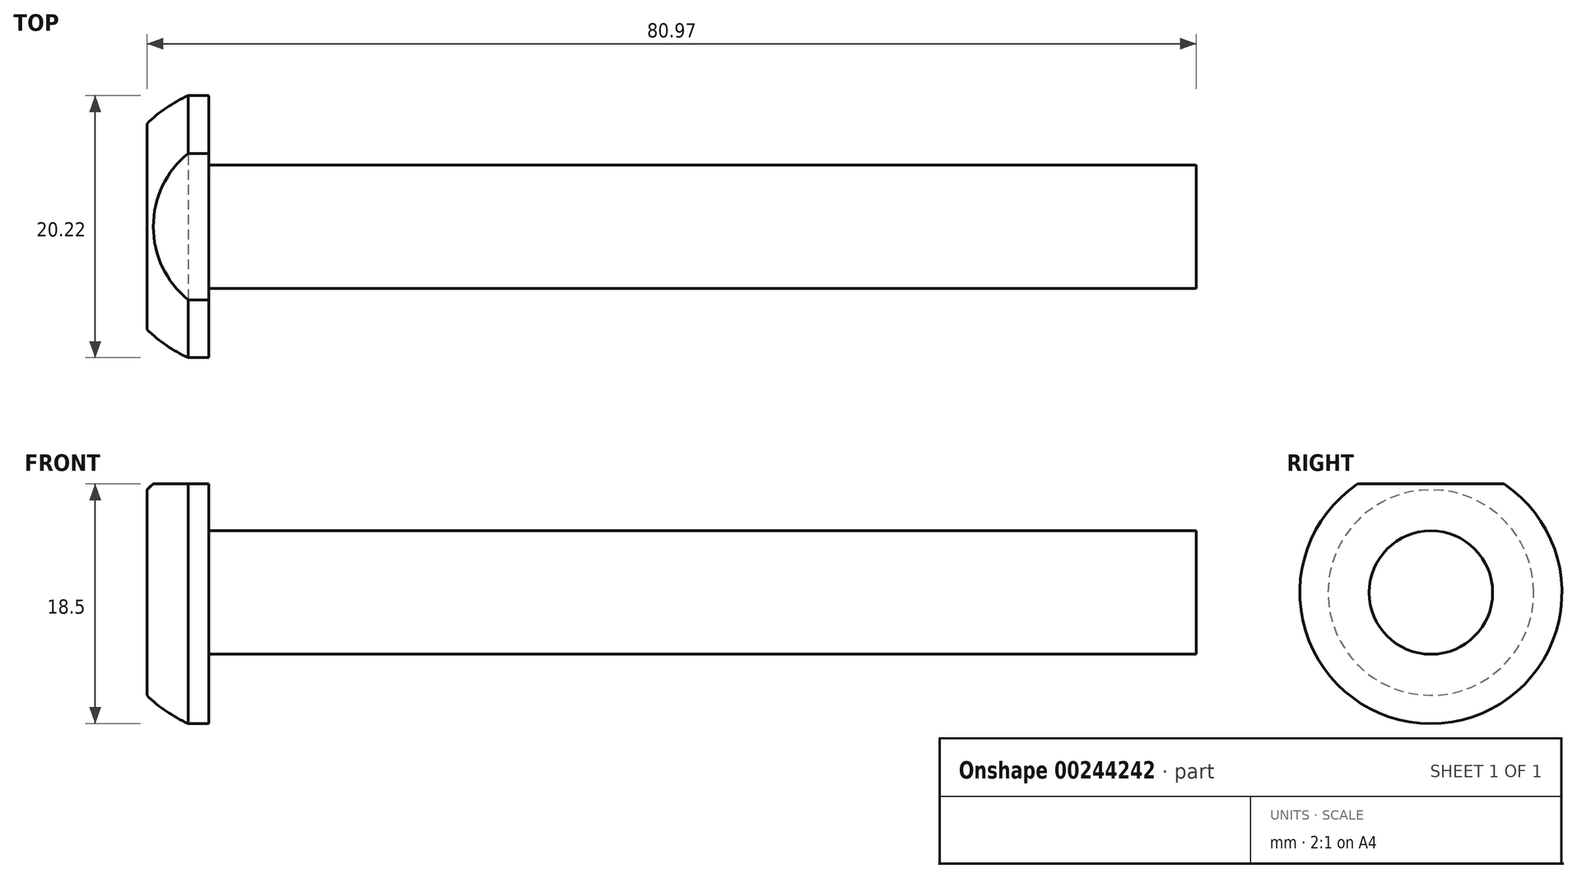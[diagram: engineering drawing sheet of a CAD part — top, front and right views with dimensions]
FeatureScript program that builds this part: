
annotation { "Feature Type Name" : "Feature", "Feature Type Description" : "" }
export const myFeature = defineFeature(function(context is Context, id is Id, definition is map)
    precondition{}
    {
        {
            var Q0;
            Q0=qCreatedBy(makeId("Front.planeOp"),FACE);
            var sketch = newSketch(context, id + "F0", { "sketchPlane" : qUnion([Q0])});
            skLineSegment(sketch, "E0.bottom", {"start": v(-52.41, 0) * mm, "end": v(23.79, 0) * mm});
            skLineSegment(sketch, "E0.top", {"start": v(-52.41, 4.76) * mm, "end": v(23.79, 4.76) * mm});
            skLineSegment(sketch, "E0.right", {"start": v(23.79, 0) * mm, "end": v(23.79, 4.76) * mm});
            skLineSegment(sketch, "E1.bottom", {"start": v(-52.41, 0) * mm, "end": v(-54, 0) * mm});
            skLineSegment(sketch, "E1.left", {"start": v(-52.41, 4.76) * mm, "end": v(-52.41, 7.94) * mm});
            skLineSegment(sketch, "E2.bottom", {"start": v(-52.41, 0) * mm, "end": v(-57.18, 0) * mm});
            skLineSegment(sketch, "E2.right", {"start": v(-57.18, 0) * mm, "end": v(-57.18, 7.94) * mm});
            skLineSegment(sketch, "E3", {"start": v(-54, 7.94) * mm, "end": v(-54, 10.11) * mm});
            skLineSegment(sketch, "E4", {"start": v(-52.41, 7.94) * mm, "end": v(-52.41, 10.11) * mm});
            skLineSegment(sketch, "E5", {"start": v(-54, 10.11) * mm, "end": v(-52.41, 10.11) * mm});
            skPoint(sketch, "E6.start.orphan", {"position": v(-54, 10.7) * mm});
            skArc(sketch, "E7.trimOffspring", {"start": v(-54, 10.11) * mm, "mid": v(-55.68, 9.16) * mm, "end": v(-57.18, 7.94) * mm});
            skLineSegment(sketch, "E8", {"start": v(-54, 7.94) * mm, "end": v(-54, 0) * mm});
            skSolve(sketch);
        }
        {
            var Q0;
            {var subQ0=sQuery(id+"F0.wireOp",EDGE,"E2.right");Q0=makeQuery(id+"F0.imprint","IMPRINT",FACE,{"disambiguationData":[TD([[makeQuery(id+"F0.imprint","IMPRINT",EDGE,{"derivedFrom":subQ0}),-1.0]])]});}
            var Q1;
            {var subQ1=sQuery(id+"F0.wireOp",EDGE,"E0.bottom");Q1=makeQuery(id+"F0.imprint","IMPRINT",FACE,{"disambiguationData":[TD([[makeQuery(id+"F0.imprint","IMPRINT",EDGE,{"derivedFrom":subQ1}),1.0]])]});}
            var Q2;
            Q2=sQuery(id+"F0.wireOp",EDGE,"E0.bottom");
            revolve(context, id + "F1", {"entities" : qUnion([Q0, Q1]), "axis" : qUnion([Q2]), "revolveType" : RevolveType.FULL});
        }
        {
            var Q0;
            Q0=makeQuery(id+"F1.opRevolve","SWEPT_FACE",FACE,{"disambiguationData":[OSD([sQuery(id+"F0.wireOp",EDGE,"E1.left"),sQuery(id+"F0.wireOp",EDGE,"E4")])]});
            var sketch = newSketch(context, id + "F2", { "sketchPlane" : qUnion([Q0])});
            skLineSegment(sketch, "E9.bottom", {"start": v(-5.65, 8.39) * mm, "end": v(6.31, 8.39) * mm});
            skLineSegment(sketch, "E9.top", {"start": v(-5.65, 10.42) * mm, "end": v(6.31, 10.42) * mm});
            skLineSegment(sketch, "E9.left", {"start": v(-5.65, 8.39) * mm, "end": v(-5.65, 10.42) * mm});
            skLineSegment(sketch, "E9.right", {"start": v(6.31, 8.39) * mm, "end": v(6.31, 10.42) * mm});
            skSolve(sketch);
        }
        {
            var Q0;
            {var subQ0=sQuery(id+"F2.wireOp",EDGE,"E9.bottom");var subQ1=makeQuery(id+"F1.opRevolve","SWEPT_EDGE",EDGE,{"disambiguationData":[OSD([sQuery(id+"F0.wireOp",EDGE,"E4"),sQuery(id+"F0.wireOp",EDGE,"E5")])]});var subQ3=makeQuery(id+"F2.imprint","INTERSECT",VERTEX,{"derivedFrom":[subQ1,subQ0]});Q0=makeQuery(id+"F2.imprint","IMPRINT",FACE,{"disambiguationData":[TD([[makeQuery(id+"F2.imprint","IMPRINT",EDGE,{"disambiguationData":[TD([[subQ3,1.0]])],"derivedFrom":subQ0}),1.0]])]});}
            extrude(context, id + "F3", {"entities" : qUnion([Q0]), "operationType" : NewBodyOperationType.REMOVE, "oppositeDirection" : true, "depth" : 25.4 * mm});
        }
    });
